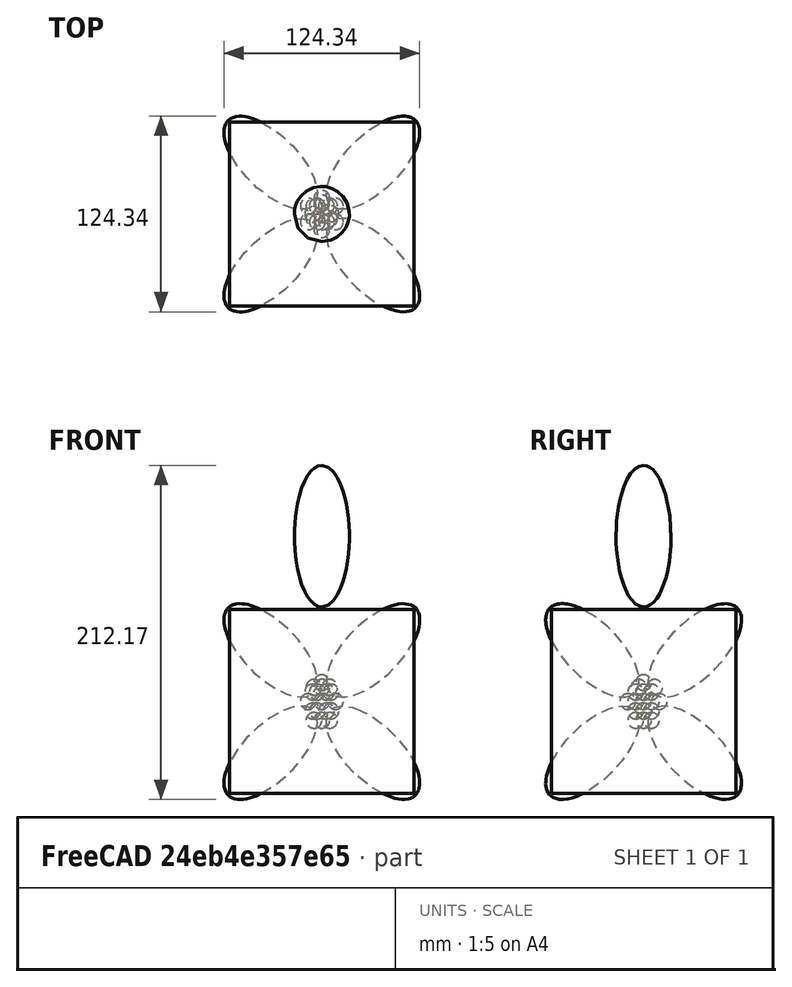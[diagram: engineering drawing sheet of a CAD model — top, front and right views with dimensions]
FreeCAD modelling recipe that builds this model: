
FCSTD DOCUMENT  (FreeCAD 0.16R6707 (Git))
Label: si-crista-unitl
License: All rights reserved
LicenseURL: http://en.wikipedia.org/wiki/All_rights_reserved
objects: Part::Part2DObjectPython×37, Part::Feature×27, Part::Sphere×9, App::DocumentObjectGroup×5, Sketcher::SketchObject×1, PartDesign::Revolution×1, Part::Box×1
note: 77 computed .brp shape members not serialized (recipe doc carries the construction recipe); baked Part::Feature solids carry a one-line shape summary decoded from their .brp

FEATURE [Part::Feature] Sphere001
  Placement = pos=(0,-10,0) rot=(0,0,1;0rad)
  shape: bbox 10 x 10 x 10 mm, 1 faces (baked)
FEATURE [Part::Feature] Sphere002
  Placement = pos=(-8.66025,-5,0) rot=(0,0,1;0rad)
  shape: bbox 10 x 10 x 10 mm, 1 faces (baked)
FEATURE [Part::Feature] Sphere003
  Placement = pos=(-8.66025,5,0) rot=(0,0,1;0rad)
  shape: bbox 10 x 10 x 10 mm, 1 faces (baked)
FEATURE [Part::Feature] Sphere004
  Placement = pos=(8.66025,-5,0) rot=(0,0,1;0rad)
  shape: bbox 10 x 10 x 10 mm, 1 faces (baked)
FEATURE [Part::Feature] Sphere005
  Placement = pos=(8.66025,5,0) rot=(0,0,1;0rad)
  shape: bbox 10 x 10 x 10 mm, 1 faces (baked)
FEATURE [Part::Feature] Sphere006
  Placement = pos=(4e-12,10,0) rot=(0,0,1;0rad)
  shape: bbox 10 x 10 x 10 mm, 1 faces (baked)
FEATURE [Part::Sphere] Sphere007  label="Centro"
  Angle1 = -90
  Angle2 = 90
  Angle3 = 360
  Radius = 5
FEATURE [Part::Feature] Sphere  label="Sphere027"
  Placement = pos=(-3,5,6) rot=(0,0,1;0rad)
  shape: bbox 10 x 10 x 10 mm, 1 faces (baked)
FEATURE [Part::Feature] Sphere008  label="Sphere028"
  Placement = pos=(2.83013,5.09808,6) rot=(0,0,1;0rad)
  shape: bbox 10 x 10 x 10 mm, 1 faces (baked)
FEATURE [Part::Feature] Sphere009  label="Sphere029"
  Placement = pos=(5.83013,0.0980762,6) rot=(0,0,1;0rad)
  shape: bbox 10 x 10 x 10 mm, 1 faces (baked)
FEATURE [Part::Feature] Sphere010  label="Sphere030"
  Placement = pos=(3,-5,6) rot=(0,0,1;0rad)
  shape: bbox 10 x 10 x 10 mm, 1 faces (baked)
FEATURE [Part::Feature] Sphere011  label="Sphere031"
  Placement = pos=(-2.83013,-5.09808,6) rot=(0,0,1;0rad)
  shape: bbox 10 x 10 x 10 mm, 1 faces (baked)
FEATURE [Part::Feature] Sphere012  label="Sphere032"
  Placement = pos=(-5.83013,-0.0980762,6) rot=(0,0,1;0rad)
  shape: bbox 10 x 10 x 10 mm, 1 faces (baked)
FEATURE [Part::Feature] Sphere013  label="Sphere033"
  Placement = pos=(-3,5,-6) rot=(0,0,1;0rad)
  shape: bbox 10 x 10 x 10 mm, 1 faces (baked)
FEATURE [Part::Feature] Sphere014  label="Sphere034"
  Placement = pos=(2.83013,5.09808,-6) rot=(0,0,1;0rad)
  shape: bbox 10 x 10 x 10 mm, 1 faces (baked)
FEATURE [Part::Feature] Sphere015  label="Sphere035"
  Placement = pos=(-2.83013,-5.09808,-6) rot=(0,0,1;0rad)
  shape: bbox 10 x 10 x 10 mm, 1 faces (baked)
FEATURE [Part::Feature] Sphere016  label="Sphere036"
  Placement = pos=(5.83013,0.0980762,-6) rot=(0,0,1;0rad)
  shape: bbox 10 x 10 x 10 mm, 1 faces (baked)
FEATURE [Part::Feature] Sphere017  label="Sphere015"
  Placement = pos=(3,-5,-6) rot=(0,0,1;0rad)
  shape: bbox 10 x 10 x 10 mm, 1 faces (baked)
FEATURE [Part::Feature] Sphere018  label="Sphere037"
  Placement = pos=(-5.83013,-0.0980762,-6) rot=(0,0,1;0rad)
  shape: bbox 10 x 10 x 10 mm, 1 faces (baked)
FEATURE [Part::Sphere] Sphere019
  Angle1 = -90
  Angle2 = 90
  Angle3 = 360
  Placement = pos=(0,0,12) rot=(0,0,1;0rad)
  Radius = 5
FEATURE [Part::Sphere] Sphere020  label="Sphere038"
  Angle1 = -90
  Angle2 = 90
  Angle3 = 360
  Placement = pos=(0,0,-12) rot=(0,0,1;0rad)
  Radius = 5
FEATURE [Part::Sphere] Sphere021  label="Sphere039"
  Angle1 = -90
  Angle2 = 90
  Angle3 = 360
  Placement = pos=(0,7,9) rot=(0,0,1;0rad)
  Radius = 5
FEATURE [Part::Sphere] Sphere022  label="Sphere040"
  Angle1 = -90
  Angle2 = 90
  Angle3 = 360
  Placement = pos=(-5,-3,9) rot=(0,0,1;0rad)
  Radius = 5
FEATURE [Part::Sphere] Sphere023  label="Sphere041"
  Angle1 = -90
  Angle2 = 90
  Angle3 = 360
  Placement = pos=(5,-3,9) rot=(0,0,1;0rad)
  Radius = 5
FEATURE [Part::Sphere] Sphere024  label="Sphere042"
  Angle1 = -90
  Angle2 = 90
  Angle3 = 360
  Placement = pos=(-5,5,-12) rot=(0,0,1;0rad)
  Radius = 5
FEATURE [Part::Sphere] Sphere025  label="Sphere043"
  Angle1 = -90
  Angle2 = 90
  Angle3 = 360
  Placement = pos=(5,5,-12) rot=(0,0,1;0rad)
  Radius = 5
FEATURE [Part::Sphere] Sphere026  label="Sphere044"
  Angle1 = -90
  Angle2 = 90
  Angle3 = 360
  Placement = pos=(0,-5,-12) rot=(0,0,1;0rad)
  Radius = 5
FEATURE [App::DocumentObjectGroup] Group  label="core"
  Group = -> [Sphere001,Sphere002,Sphere003,Sphere004,Sphere005,Sphere006,Sphere,Sphere008,Sphere009,Sphere010,Sphere011,Sphere012,Sphere013,Sphere014,Sphere015,Sphere016,Sphere017,Sphere018,Sphere019,Sphere020,Sphere021,Sphere022,Sphere023,Sphere024,Sphere025,Sphere026]
FEATURE [Part::Part2DObjectPython] Line  # Draft 2D object (typed FeaturePython)
  ChamferSize = 0
  Closed = false
  End = (0.452401,-0.175885,80)
  FilletRadius = 0
  Length = 80
  MakeFace = true
  Points = (2) [(0.452401,-0.175885,0),(0.452401,-0.175885,80)]
  Start = (0.452401,-0.175885,0)
  Subdivisions = 0
FEATURE [Part::Part2DObjectPython] Arc  # Draft 2D object (typed FeaturePython)
  FirstAngle = -171.133
  LastAngle = -90
  MakeFace = true
  Placement = pos=(-25,43.3013,0) rot=(0,0,1;0rad)
  Radius = 86.6025
FEATURE [Part::Part2DObjectPython] Arc001  # Draft 2D object (typed FeaturePython)
  FirstAngle = 90
  LastAngle = 169.455
  MakeFace = true
  Placement = pos=(-25,-43.3013,0) rot=(0,0,1;0rad)
  Radius = 86.6025
FEATURE [Part::Part2DObjectPython] Line001  # Draft 2D object (typed FeaturePython)
  ChamferSize = 0
  Closed = false
  End = (-25,0,0)
  FilletRadius = 0
  Length = 75
  MakeFace = true
  Points = (2) [(-100,0,0),(-25,-2.13163e-14,0)]
  Start = (-100,0,0)
  Subdivisions = 0
FEATURE [Part::Part2DObjectPython] Arc002  # Draft 2D object (typed FeaturePython)
  FirstAngle = 52.9075
  LastAngle = 180
  MakeFace = true
  Placement = pos=(-25,0,0) rot=(1,0,0;1.5708rad)
  Radius = 75
FEATURE [Part::Part2DObjectPython] Line006  # Draft 2D object (typed FeaturePython)
  ChamferSize = 0
  Closed = false
  End = (50,0,0)
  FilletRadius = 0
  Length = 58.8303
  MakeFace = true
  Points = (2) [(0,0,31),(50,1.53081e-15,0)]
  Start = (0,0,31)
  Subdivisions = 0
FEATURE [Part::Part2DObjectPython] Line007  # Draft 2D object (typed FeaturePython)
  ChamferSize = 0
  Closed = false
  End = (1.07885,0,70.9091)
  FilletRadius = 0
  Length = 39.9237
  MakeFace = true
  Points = (2) [(0,0,31),(1.07885,0,70.9091)]
  Start = (0,0,31)
  Subdivisions = 0
FEATURE [Part::Part2DObjectPython] Line008  # Draft 2D object (typed FeaturePython)
  ChamferSize = 0
  Closed = false
  End = (-25,43.3013,0)
  FilletRadius = 0
  Length = 58.8303
  MakeFace = true
  Points = (2) [(0,0,31),(-25,43.3013,0)]
  Start = (0,0,31)
  Subdivisions = 0
FEATURE [Sketcher::SketchObject] Sketch
  Placement = pos=(0,0,0) rot=(1,0,0;1.5708rad)
  sketch-geometry (6):
    g0: LineSegment StartX=0 StartY=60 StartZ=0 EndX=0 EndY=150 EndZ=0
    g1: ArcOfEllipse CenterX=0 CenterY=105 CenterZ=0 NormalX=0 NormalY=0 NormalZ=1 MajorRadius=45 MinorRadius=17.5 AngleXU=1.5708 StartAngle=3.14159 EndAngle=6.28319
    g2: LineSegment [constr] StartX=0 StartY=150 StartZ=0 EndX=0 EndY=60 EndZ=0
    g3: LineSegment [constr] StartX=-17.5 StartY=105 StartZ=0 EndX=17.5 EndY=105 EndZ=0
    g4: GeomPoint [constr] X=0 Y=146.458 Z=0
    g5: GeomPoint [constr] X=0 Y=63.5422 Z=0
  constraints (10):
    c: PointOnObject(g0,g-2)
    c: PointOnObject(g0,g-2)
    c: InternalAlignment(g2-g5 -> g1) x4
    c: Coincident(g2,g0)
    c: Coincident(g1,g0)
    c: Coincident(g2,g0)
    c: DistanceX(g3,g3) = 35
    c: DistanceY(g-1,g0) = 60
    c: DistanceY(g0,g0) = 90
    c: Coincident(g1,g0)
FEATURE [PartDesign::Revolution] Revolution001  label="orbital-1"
  Angle = 360
  Axis = (0,0,1)
  Base = (0,0,0)
  Placement = pos=(0,0,0) rot=(1,0,0;1.5708rad)
  ReferenceAxis = -> Sketch [V_Axis]
  Reversed = true
  Sketch = -> Sketch
FEATURE [Part::Feature] Face
  shape: bbox 40.2 x 69.18 x 91.71 mm, 1 faces, 0 solids (baked)
FEATURE [Part::Part2DObjectPython] Arc003  # Draft 2D object (typed FeaturePython)
  FirstAngle = -223.482
  LastAngle = -86.8237
  MakeFace = true
  Placement = pos=(0,0,31) rot=(-0.761669,-0.469136,0.446958;1.79277rad)
  Radius = 39.9237
FEATURE [Part::Part2DObjectPython] Line010  # Draft 2D object (typed FeaturePython)
  ChamferSize = 0
  Closed = false
  End = (68.0246,117.822,115.351)
  FilletRadius = 0
  Length = 200
  MakeFace = true
  Points = (2) [(-16.9656,-29.3853,9.96263),(68.0246,117.822,115.351)]
  Start = (-16.9656,-29.3853,9.96263)
  Subdivisions = 0
FEATURE [Part::Part2DObjectPython] Line005  # Draft 2D object (typed FeaturePython)
  ChamferSize = 0
  Closed = false
  End = (-25,-43.3013,0)
  FilletRadius = 0
  Length = 58.8303
  MakeFace = true
  Points = (2) [(0,0,31),(-25,-43.3013,0)]
  Start = (0,0,31)
  Subdivisions = 0
  Support = -> Sphere005
FEATURE [App::DocumentObjectGroup] Group002  label="Aux"
  Group = -> [Line,Arc,Arc001,Line001,Arc002,Line006,Line007,Line008,Face,Arc003,Line010,Line005]
FEATURE [App::DocumentObjectGroup] Group003  label="Orbital-src"
  Group = -> [Revolution001]
FEATURE [Part::Feature] Revolution001001  label="orbital-005"
  Placement = pos=(-93.141,-93.141,-93.141) rot=(0.774597,0.447214,-0.447214;1.07959rad)
  shape: bbox 59.27 x 59.27 x 59.3 mm, 1 faces (baked)
FEATURE [Part::Feature] Clone003  label="orbital-006"
  Placement = pos=(28.1025,-28.1025,-28.1025) rot=(0.706389,0.001957,0.707821;0.955319rad)
  shape: bbox 59.27 x 59.3 x 59.27 mm, 1 faces (baked)
FEATURE [Part::Feature] Clone004  label="orbital-007"
  Placement = pos=(93.141,-93.141,93.141) rot=(-0.765198,0.217596,0.605907;0.980817rad)
  shape: bbox 59.29 x 59.29 x 59.24 mm, 1 faces (baked)
FEATURE [Part::Feature] Clone005  label="orbital-008"
  Placement = pos=(93.141,93.141,-93.141) rot=(-0.447501,0.44725,0.77441;2.90341rad)
  shape: bbox 59.3 x 59.27 x 59.27 mm, 1 faces (baked)
FEATURE [App::DocumentObjectGroup] Group004  label="Orbitales"
  Group = -> [Revolution001001,Clone003,Clone004,Clone005]
FEATURE [Part::Part2DObjectPython] Line011  # Draft 2D object (typed FeaturePython)
  ChamferSize = 0
  Closed = false
  End = (86.973,-1.52113,-22.4487)
  FilletRadius = 0
  Length = 179.005
  MakeFace = true
  Points = (2) [(4.28626e-15,9.99201e-14,134),(86.973,-1.52113,-22.4487)]
  Start = (0,0,134)
  Subdivisions = 0
FEATURE [Part::Part2DObjectPython] Line012  # Draft 2D object (typed FeaturePython)
  ChamferSize = 0
  Closed = false
  End = (-42.1692,76.0814,-22.4487)
  FilletRadius = 0
  Length = 152.695
  MakeFace = true
  Points = (2) [(-41.2006,-76.6102,-22.4487),(-42.1692,76.0814,-22.4487)]
  Start = (-41.2006,-76.6102,-22.4487)
  Subdivisions = 0
FEATURE [Part::Part2DObjectPython] Line013  # Draft 2D object (typed FeaturePython)
  ChamferSize = 0
  Closed = false
  End = (43.0022,75.5852,55.7756)
  FilletRadius = 0
  Length = 152.695
  MakeFace = true
  Placement = pos=(85.1714,-0.496142,78.2244) rot=(0,0,1;0rad)
  Points = (2) [(-41.2006,-76.6102,-22.4487),(-42.1692,76.0814,-22.4487)]
  Start = (43.9708,-77.1064,55.7756)
  Subdivisions = 0
FEATURE [Part::Part2DObjectPython] Line014  # Draft 2D object (typed FeaturePython)
  ChamferSize = 0
  Closed = false
  End = (1.80162,-1.02498,-100.673)
  FilletRadius = 0
  Length = 179.005
  MakeFace = true
  Placement = pos=(-85.1714,0.496142,-78.2244) rot=(0,0,1;0rad)
  Points = (2) [(4.28626e-15,9.99201e-14,134),(86.973,-1.52113,-22.4487)]
  Start = (-85.1714,0.496142,55.7756)
  Subdivisions = 0
FEATURE [Part::Part2DObjectPython] Line015  # Draft 2D object (typed FeaturePython)
  ChamferSize = 0
  Closed = false
  End = (86.973,-1.52113,-22.4487)
  FilletRadius = 0
  Length = 116.967
  MakeFace = true
  Points = (2) [(43.9708,-77.1064,55.7756),(86.973,-1.52113,-22.4487)]
  Start = (43.9708,-77.1064,55.7756)
  Subdivisions = 0
FEATURE [Part::Part2DObjectPython] DWire  # Draft 2D object (typed FeaturePython)
  ChamferSize = 0
  Closed = false
  End = (43.9708,-77.1064,55.7756)
  FilletRadius = 0
  Length = 353.593
  MakeFace = true
  Points = (4) [(86.973,-1.52113,-22.4487),(43.0022,75.5852,55.7756),(4.28626e-15,9.99201e-14,134),(43.9708,-77.1064,55.7756)]
  Start = (86.973,-1.52113,-22.4487)
  Subdivisions = 0
FEATURE [Part::Part2DObjectPython] DWire001  # Draft 2D object (typed FeaturePython)
  ChamferSize = 0
  Closed = true
  End = (-85.1714,0.496142,55.7756)
  FilletRadius = 0
  Length = 470.56
  MakeFace = false
  Points = (4) [(-41.2006,-76.6102,-22.4487),(1.80162,-1.02498,-100.673),(-42.1692,76.0814,-22.4487),(-85.1714,0.496142,55.7756)]
  Start = (-41.2006,-76.6102,-22.4487)
  Subdivisions = 0
FEATURE [Part::Part2DObjectPython] Line016  # Draft 2D object (typed FeaturePython)
  ChamferSize = 0
  Closed = false
  End = (-41.2006,-76.6102,-22.4487)
  FilletRadius = 0
  Length = 115.644
  MakeFace = true
  Points = (2) [(43.9708,-77.1064,55.7756),(-41.2006,-76.6102,-22.4487)]
  Start = (43.9708,-77.1064,55.7756)
  Subdivisions = 0
FEATURE [Part::Part2DObjectPython] Line017  # Draft 2D object (typed FeaturePython)
  ChamferSize = 0
  Closed = false
  End = (0,0,134)
  FilletRadius = 0
  Length = 115.644
  MakeFace = true
  Points = (2) [(-85.1714,0.496142,55.7756),(5.69585e-15,9.9698e-14,134)]
  Start = (-85.1714,0.496142,55.7756)
  Subdivisions = 0
FEATURE [Part::Part2DObjectPython] Line018  # Draft 2D object (typed FeaturePython)
  ChamferSize = 0
  Closed = false
  End = (43.0022,75.5852,55.7756)
  FilletRadius = 0
  Length = 115.644
  MakeFace = true
  Points = (2) [(-42.1692,76.0814,-22.4487),(43.0022,75.5852,55.7756)]
  Start = (-42.1692,76.0814,-22.4487)
  Subdivisions = 0
FEATURE [Part::Part2DObjectPython] Line019  # Draft 2D object (typed FeaturePython)
  ChamferSize = 0
  Closed = false
  End = (86.973,-1.52113,-22.4487)
  FilletRadius = 0
  Length = 115.644
  MakeFace = true
  Points = (2) [(1.80162,-1.02498,-100.673),(86.973,-1.52113,-22.4487)]
  Start = (1.80162,-1.02498,-100.673)
  Subdivisions = 0
FEATURE [Part::Box] Box  label="Cube"
  Height = 117
  Length = 117
  Placement = pos=(-58.5,-58.5,-58.5) rot=(0,0,1;0rad)
  Width = 117
FEATURE [Part::Part2DObjectPython] Line020  # Draft 2D object (typed FeaturePython)
  ChamferSize = 0
  Closed = false
  End = (-58.5,58.5,58.5)
  FilletRadius = 0
  Length = 101.325
  MakeFace = true
  Points = (2) [(0,0,0),(-58.5,58.5,58.5)]
  Start = (0,0,0)
  Subdivisions = 0
FEATURE [Part::Part2DObjectPython] Line021  # Draft 2D object (typed FeaturePython)
  ChamferSize = 0
  Closed = false
  End = (-58.5,-58.5,-58.5)
  FilletRadius = 0
  Length = 101.325
  MakeFace = true
  Points = (2) [(0,0,0),(-58.5,-58.5,-58.5)]
  Start = (0,0,0)
  Subdivisions = 0
FEATURE [Part::Part2DObjectPython] Line023  # Draft 2D object (typed FeaturePython)
  ChamferSize = 0
  Closed = false
  End = (58.5,58.5,-58.5)
  FilletRadius = 0
  Length = 101.325
  MakeFace = true
  Points = (2) [(0,0,0),(58.5,58.5,-58.5)]
  Start = (0,0,0)
  Subdivisions = 0
FEATURE [Part::Part2DObjectPython] Line024  # Draft 2D object (typed FeaturePython)
  ChamferSize = 0
  Closed = false
  End = (58.5,-58.5,58.5)
  FilletRadius = 0
  Length = 101.325
  MakeFace = true
  Points = (2) [(0,0,0),(58.5,-58.5,58.5)]
  Start = (0,0,0)
  Subdivisions = 0
FEATURE [Part::Part2DObjectPython] DWire002  # Draft 2D object (typed FeaturePython)
  ChamferSize = 0
  Closed = false
  End = (58.5,-58.5,58.5)
  FilletRadius = 0
  Length = 661.852
  MakeFace = true
  Points = (5) [(-58.5,-58.5,-58.5),(58.5,-58.5,58.5),(-58.5,58.5,58.5),(58.5,58.5,-58.5),(58.5,-58.5,58.5)]
  Start = (-58.5,-58.5,-58.5)
  Subdivisions = 0
FEATURE [Part::Part2DObjectPython] Line025  # Draft 2D object (typed FeaturePython)
  ChamferSize = 0
  Closed = false
  End = (-58.5,58.5,58.5)
  FilletRadius = 0
  Length = 165.463
  MakeFace = true
  Points = (2) [(-58.5,-58.5,-58.5),(-58.5,58.5,58.5)]
  Start = (-58.5,-58.5,-58.5)
  Subdivisions = 0
FEATURE [Part::Part2DObjectPython] Line026  # Draft 2D object (typed FeaturePython)
  ChamferSize = 0
  Closed = false
  End = (58.5,58.5,-58.5)
  FilletRadius = 0
  Length = 165.463
  MakeFace = true
  Points = (2) [(-58.5,-58.5,-58.5),(58.5,58.5,-58.5)]
  Start = (-58.5,-58.5,-58.5)
  Subdivisions = 0
FEATURE [App::DocumentObjectGroup] Group001  label="tetrahedron"
  Group = -> [Line025,Line026,DWire002]
FEATURE [Part::Part2DObjectPython] Line027  # Draft 2D object (typed FeaturePython)
  ChamferSize = 0
  Closed = false
  End = (95.4093,-8.47099,-11.0385)
  FilletRadius = 0
  Length = 96.4185
  MakeFace = true
  Points = (2) [(0,0,0),(95.4093,-8.47099,-11.0385)]
  Start = (0,0,0)
  Subdivisions = 0
FEATURE [Part::Part2DObjectPython] Line028  # Draft 2D object (typed FeaturePython)
  ChamferSize = 0
  Closed = false
  End = (95.4093,-8.47099,-11.0385)
  FilletRadius = 0
  Length = 90
  MakeFace = true
  Points = (2) [(58.5,58.5,-58.5),(95.4093,-8.47099,-11.0385)]
  Start = (58.5,58.5,-58.5)
  Subdivisions = 0
  Support = -> Clone005
FEATURE [Part::Feature] Face001
  shape: bbox 142.5 x 108.5 x 92.23 mm, 1 faces, 0 solids (baked)
FEATURE [Part::Part2DObjectPython] Line029  # Draft 2D object (typed FeaturePython)
  ChamferSize = 0
  Closed = false
  End = (-17.9532,-56.9789,105.961)
  FilletRadius = 0
  Length = 121.642
  MakeFace = true
  Points = (2) [(0,0,0),(-17.9532,-56.9789,105.961)]
  Start = (0,0,0)
  Subdivisions = 0
FEATURE [Part::Part2DObjectPython] Line030  # Draft 2D object (typed FeaturePython)
  ChamferSize = 0
  Closed = false
  End = (-17.9532,-56.9789,105.961)
  FilletRadius = 0
  Length = 90
  MakeFace = true
  Points = (2) [(58.5,-58.5,58.5),(-17.9532,-56.9789,105.961)]
  Start = (58.5,-58.5,58.5)
  Subdivisions = 0
  Support = -> Clone004
FEATURE [Part::Feature] Face002
  shape: bbox 87.72 x 92.87 x 125.7 mm, 1 faces, 0 solids (baked)
FEATURE [Part::Part2DObjectPython] Line031  # Draft 2D object (typed FeaturePython)
  ChamferSize = 0
  Closed = false
  End = (0,0,0)
  FilletRadius = 0
  Length = 95.9215
  MakeFace = true
  Points = (2) [(-94.8807,-8.75957,11.0385),(0,0,0)]
  Start = (-94.8807,-8.75957,11.0385)
  Subdivisions = 0
FEATURE [Part::Part2DObjectPython] Line032  # Draft 2D object (typed FeaturePython)
  ChamferSize = 0
  Closed = false
  End = (-58.5,58.5,58.5)
  FilletRadius = 0
  Length = 90
  MakeFace = true
  Points = (2) [(-94.8807,-8.75957,11.0385),(-58.5,58.5,58.5)]
  Start = (-94.8807,-8.75957,11.0385)
  Subdivisions = 0
  Support = -> Clone003
FEATURE [Part::Feature] Face003
  shape: bbox 142.5 x 109.1 x 91.98 mm, 1 faces, 0 solids (baked)
FEATURE [Part::Part2DObjectPython] Line033  # Draft 2D object (typed FeaturePython)
  ChamferSize = 0
  Closed = false
  End = (0,0,0)
  FilletRadius = 0
  Length = 88.5254
  MakeFace = true
  Points = (2) [(-58.5,-58.5,31.5),(0,0,0)]
  Start = (-58.5,-58.5,31.5)
  Subdivisions = 0
FEATURE [Part::Part2DObjectPython] Line034  # Draft 2D object (typed FeaturePython)
  ChamferSize = 0
  Closed = false
  End = (-58.5,-58.5,31.5)
  FilletRadius = 0
  Length = 90
  MakeFace = true
  Points = (2) [(-58.5,-58.5,-58.5),(-58.5,-58.5,31.5)]
  Start = (-58.5,-58.5,-58.5)
  Subdivisions = 0
  Support = -> Revolution001001
FEATURE [Part::Feature] Face004
  shape: bbox 98.2 x 98.2 x 133.7 mm, 1 faces, 0 solids (baked)
